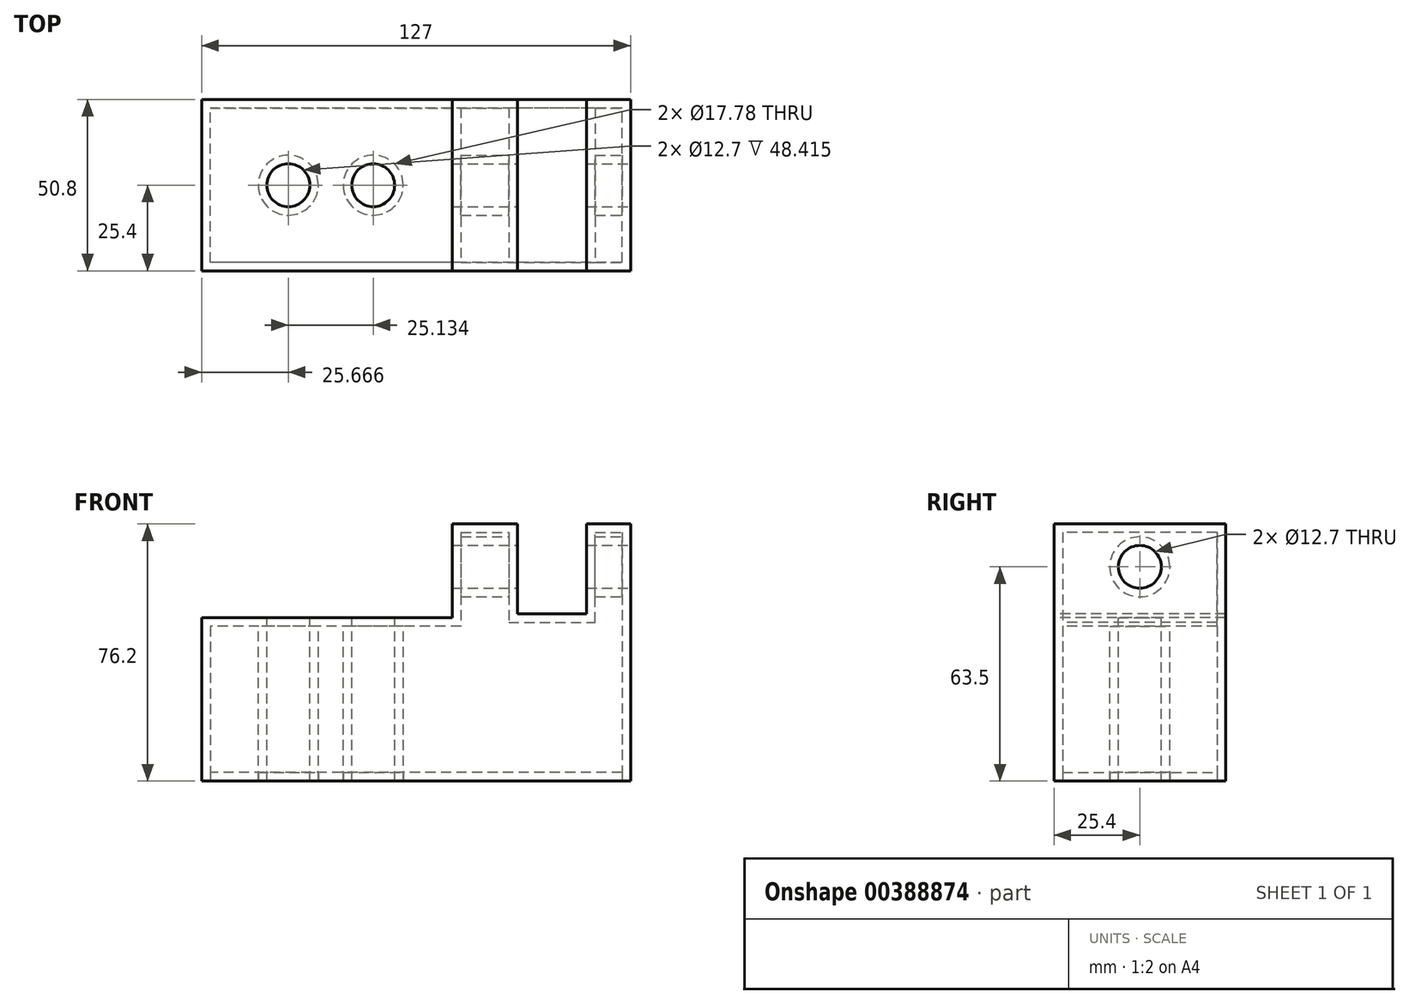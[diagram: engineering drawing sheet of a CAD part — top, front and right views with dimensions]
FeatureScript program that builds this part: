
annotation { "Feature Type Name" : "Feature", "Feature Type Description" : "" }
export const myFeature = defineFeature(function(context is Context, id is Id, definition is map)
    precondition{}
    {
        {
            var Q0;
            Q0=qCreatedBy(makeId("Front.planeOp"),FACE);
            var sketch = newSketch(context, id + "F0", { "sketchPlane" : qUnion([Q0])});
            skLineSegment(sketch, "E0", {"start": v(0, 76.2) * mm, "end": v(127, 76.2) * mm});
            skLineSegment(sketch, "E1", {"start": v(127, 76.2) * mm, "end": v(127, 0) * mm});
            skLineSegment(sketch, "E2", {"start": v(127, 0) * mm, "end": v(0, 0) * mm});
            skLineSegment(sketch, "E3", {"start": v(0, 76.2) * mm, "end": v(0, 0) * mm});
            skSolve(sketch);
        }
        {
            var Q0;
            Q0=makeQuery(id+"F0.imprint","IMPRINT",FACE,{"disambiguationData":[TD([[makeQuery(id+"F0.imprint","IMPRINT",EDGE,{"derivedFrom":sQuery(id+"F0.wireOp",EDGE,"E0")}),-1.0]])]});
            extrude(context, id + "F1", {"entities" : qUnion([Q0]), "depth" : 50.8 * mm});
        }
        {
            var Q0;
            Q0=makeQuery(id+"F1.opExtrude","CAP_FACE",FACE,{"disambiguationData":[OSD([sQuery(id+"F0.wireOp",EDGE,"E0"),sQuery(id+"F0.wireOp",EDGE,"E1"),sQuery(id+"F0.wireOp",EDGE,"E2"),sQuery(id+"F0.wireOp",EDGE,"E3")])],"isStart":false});
            var sketch = newSketch(context, id + "F2", { "sketchPlane" : qUnion([Q0])});
            skLineSegment(sketch, "E4", {"start": v(93.47, 76.2) * mm, "end": v(93.47, 49.6) * mm});
            skLineSegment(sketch, "E5", {"start": v(93.47, 49.6) * mm, "end": v(113.99, 49.6) * mm});
            skLineSegment(sketch, "E6", {"start": v(113.99, 49.6) * mm, "end": v(113.99, 76.2) * mm});
            skSolve(sketch);
        }
        {
            var Q0;
            {var subQ0=sQuery(id+"F2.wireOp",EDGE,"E4");Q0=makeQuery(id+"F2.imprint","IMPRINT",FACE,{"disambiguationData":[TD([[makeQuery(id+"F2.imprint","IMPRINT",EDGE,{"derivedFrom":subQ0}),1.0]])]});}
            extrude(context, id + "F3", {"entities" : qUnion([Q0]), "operationType" : NewBodyOperationType.REMOVE, "endBound" : BoundingType.UP_TO_NEXT, "oppositeDirection" : true, "depth" : 25.4 * mm});
        }
        {
            var Q0;
            {var subQ2=sQuery(id+"F2.wireOp",EDGE,"E4");Q0=makeQuery(id+"F2.imprint","IMPRINT",FACE,{"disambiguationData":[TD([[makeQuery(id+"F2.imprint","IMPRINT",EDGE,{"derivedFrom":subQ2}),-1.0]])]});}
            var sketch = newSketch(context, id + "F4", { "sketchPlane" : qUnion([Q0])});
            skLineSegment(sketch, "E7", {"start": v(74.23, 76.2) * mm, "end": v(74.23, 48.42) * mm});
            skLineSegment(sketch, "E8", {"start": v(74.23, 48.42) * mm, "end": v(0, 48.42) * mm});
            skLineSegment(sketch, "E9.0", {"start": v(0, 76.2) * mm, "end": v(93.47, 76.2) * mm});
            skPoint(sketch, "E10", {"position": v(74.23, 76.2) * mm});
            skPoint(sketch, "E11", {"position": v(0, 48.42) * mm});
            skSolve(sketch);
        }
        {
            var Q0;
            {var subQ0=sQuery(id+"F4.wireOp",EDGE,"E7");Q0=makeQuery(id+"F4.imprint","IMPRINT",FACE,{"disambiguationData":[TD([[makeQuery(id+"F4.imprint","IMPRINT",EDGE,{"derivedFrom":subQ0}),-1.0]])]});}
            extrude(context, id + "F5", {"entities" : qUnion([Q0]), "operationType" : NewBodyOperationType.REMOVE, "endBound" : BoundingType.UP_TO_NEXT, "oppositeDirection" : true, "depth" : 25.4 * mm});
        }
        {
            var Q0;
            Q0=makeQuery(id+"F1.opExtrude","SWEPT_FACE",FACE,{"disambiguationData":[OSD([sQuery(id+"F0.wireOp",EDGE,"E1")])]});
            var sketch = newSketch(context, id + "F6", { "sketchPlane" : qUnion([Q0])});
            skCircle(sketch, "E12", {"center": v(-25.4, 63.5) * mm, "radius": 6.35 * mm});
            skLineSegment(sketch, "E13.0", {"start": v(-50.8, 76.2) * mm, "end": v(0, 76.2) * mm});
            skSolve(sketch);
        }
        {
            var Q0;
            Q0=makeQuery(id+"F6.imprint","IMPRINT",FACE,{"disambiguationData":[TD([[makeQuery(id+"F6.imprint","IMPRINT",EDGE,{"derivedFrom":sQuery(id+"F6.wireOp",EDGE,"E12")}),1.0]])]});
            var Q1;
            Q1=makeQuery(id+"F5.boolean.opBoolean","COPY",FACE,{"derivedFrom":makeQuery(id+"F5.opExtrude","SWEPT_FACE",FACE,{"disambiguationData":[OSD([sQuery(id+"F4.wireOp",EDGE,"E7")])]})});
            extrude(context, id + "F7", {"entities" : qUnion([Q0]), "operationType" : NewBodyOperationType.REMOVE, "endBound" : BoundingType.THROUGH_ALL, "oppositeDirection" : true, "endBoundEntityFace" : qUnion([Q1]), "depth" : 25.4 * mm});
        }
        {
            var Q0;
            Q0=makeQuery(id+"F5.boolean.opBoolean","COPY",FACE,{"derivedFrom":makeQuery(id+"F5.opExtrude","SWEPT_FACE",FACE,{"disambiguationData":[OSD([sQuery(id+"F4.wireOp",EDGE,"E8")])]})});
            var sketch = newSketch(context, id + "F8", { "sketchPlane" : qUnion([Q0])});
            skCircle(sketch, "E14", {"center": v(50.8, -25.4) * mm, "radius": 6.35 * mm});
            skSolve(sketch);
        }
        {
            var Q0;
            Q0 = qSketchRegion(id + "F8", true);
            extrude(context, id + "F9", {"entities" : qUnion([Q0]), "operationType" : NewBodyOperationType.REMOVE, "endBound" : BoundingType.UP_TO_NEXT, "oppositeDirection" : true, "depth" : 25.4 * mm});
        }
        {
            var Q0;
            Q0=makeQuery(id+"F5.boolean.opBoolean","COPY",FACE,{"derivedFrom":makeQuery(id+"F5.opExtrude","SWEPT_FACE",FACE,{"disambiguationData":[OSD([sQuery(id+"F4.wireOp",EDGE,"E8")])]})});
            var sketch = newSketch(context, id + "F10", { "sketchPlane" : qUnion([Q0])});
            skCircle(sketch, "E15", {"center": v(25.67, -25.4) * mm, "radius": 6.35 * mm});
            skSolve(sketch);
        }
        {
            var Q0;
            Q0=makeQuery(id+"F10.imprint","IMPRINT",FACE,{"disambiguationData":[TD([[makeQuery(id+"F10.imprint","IMPRINT",EDGE,{"derivedFrom":sQuery(id+"F10.wireOp",EDGE,"E15")}),1.0]])]});
            extrude(context, id + "F11", {"entities" : qUnion([Q0]), "operationType" : NewBodyOperationType.REMOVE, "endBound" : BoundingType.UP_TO_NEXT, "oppositeDirection" : true, "depth" : 25.4 * mm});
        }
        {
            var Q0;
            Q0=makeQuery(id+"F1.opExtrude","SWEPT_FACE",FACE,{"disambiguationData":[OSD([sQuery(id+"F0.wireOp",EDGE,"E2")])]});
            cPlane(context, id + "F12", {"entities" : qUnion([Q0]), "cplaneType" : CPlaneType.OFFSET, "offset" : 0 * mm, "width" : 152.4 * mm, "height" : 152.4 * mm});
        }
        {
            var Q0;
            Q0=makeQuery(id+"F1.opExtrude","SWEPT_FACE",FACE,{"disambiguationData":[OSD([sQuery(id+"F0.wireOp",EDGE,"E2")])]});
            shell(context, id + "F13", {"entities" : qUnion([Q0]), "thickness" : 2.54 * mm});
        }
        {
            var Q0;
            Q0=qCreatedBy(id+"F12.planeOp",FACE);
            var sketch = newSketch(context, id + "F14", { "sketchPlane" : qUnion([Q0])});
            skCircle(sketch, "E16.0", {"center": v(50.8, 25.4) * mm, "radius": 8.9 * mm});
            skCircle(sketch, "E17.0", {"center": v(25.67, 25.4) * mm, "radius": 8.9 * mm});
            skLineSegment(sketch, "E18.0", {"start": v(124.46, 48.26) * mm, "end": v(2.54, 48.26) * mm});
            skLineSegment(sketch, "E19.0", {"start": v(124.46, 48.26) * mm, "end": v(124.46, 2.54) * mm});
            skLineSegment(sketch, "E20.0", {"start": v(124.46, 2.54) * mm, "end": v(2.54, 2.54) * mm});
            skLineSegment(sketch, "E21.0", {"start": v(2.54, 48.26) * mm, "end": v(2.54, 2.54) * mm});
            skSolve(sketch);
        }
        {
            var Q0;
            Q0 = qSketchRegion(id + "F14", true);
            extrude(context, id + "F15", {"entities" : qUnion([Q0]), "oppositeDirection" : true, "depth" : 2.54 * mm});
        }
    });
